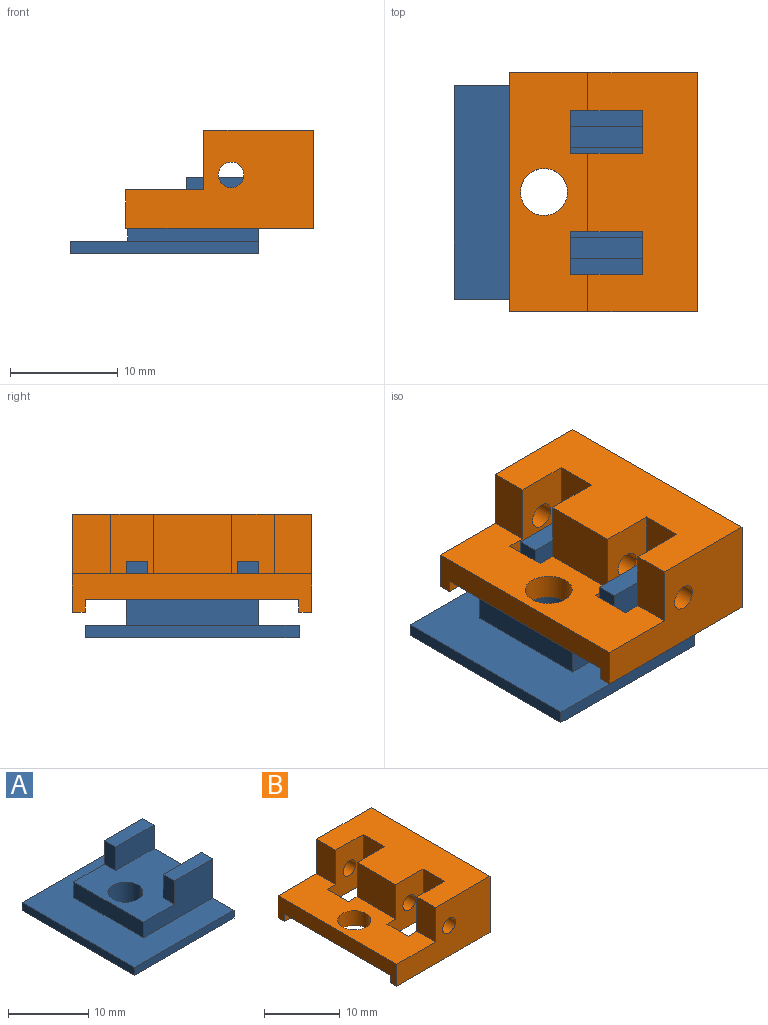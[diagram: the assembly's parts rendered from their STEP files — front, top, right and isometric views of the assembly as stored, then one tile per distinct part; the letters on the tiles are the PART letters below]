
ASSEMBLY  parts=2 mates=1
PART A: 17 faces, bbox 17.5x19.8x7.1 mm
  f0: plane 19.84x17.51mm, normal (0,0,1), area 197.6mm2, adj f1,f2,f3,f4,f7,f13,f15
  f1: plane 19.84x7.14mm, normal (1,0,0), area 67.1mm2, adj f0,f2,f4,f6,f7,f9,f10,f11
  f2: plane 17.51x1.19mm, normal (0,1,0), area 20.9mm2, adj f0,f1,f3,f6
  f3: plane 19.84x1.19mm, normal (-1,0,0), area 23.6mm2, adj f0,f2,f4,f6
  f4: plane 17.51x1.19mm, normal (0,-1,0), area 20.9mm2, adj f0,f1,f3,f6
  f5: cylinder r=2.18mm len=4.37mm, axis (0,0,-1), area 49mm2, adj f6,f16
  f6: plane 19.84x17.51mm, normal (0,0,-1), area 332.6mm2, adj f1,f2,f3,f4,f5
  f7: plane 12.18x5.95mm, normal (0,1,0), area 53.1mm2, adj f0,f1,f8,f10,f15,f16
  f8: plane 3.57x1.98mm, normal (-1,0,0), area 7.1mm2, adj f7,f9,f10,f16
  f9: plane 6.75x3.57mm, normal (0,-1,0), area 24.1mm2, adj f1,f8,f10,f16
  f10: plane 6.75x1.98mm, normal (0,0,1), area 13.4mm2, adj f1,f7,f8,f9
  f11: plane 6.75x3.57mm, normal (0,1,0), area 24.1mm2, adj f1,f12,f14,f16
  f12: plane 3.57x1.98mm, normal (-1,0,0), area 7.1mm2, adj f11,f13,f14,f16
  f13: plane 12.18x5.95mm, normal (0,-1,0), area 53.1mm2, adj f0,f1,f12,f14,f15,f16
  f14: plane 6.75x1.98mm, normal (0,0,1), area 13.4mm2, adj f1,f11,f12,f13
  f15: plane 12.3x2.38mm, normal (-1,0,0), area 29.3mm2, adj f0,f7,f13,f16
  f16: plane 12.3x12.18mm, normal (0,0,1), area 108.2mm2, adj f1,f5,f7,f8,f9,f11,f12,f13
PART B: 26 faces, bbox 17.5x22.2x9.1 mm
  f0: plane 22.23x7.25mm, normal (0,0,1), area 133.1mm2, adj f1,f2,f5,f6,f7,f8,f11,f12
  f1: plane 7.94x6.75mm, normal (0,-1,0), area 40mm2, adj f0,f3,f4,f6,f15,f16,f25
  f2: plane 7.94x6.75mm, normal (0,1,0), area 40mm2, adj f0,f3,f7,f9,f15,f16,f25
  f3: plane 19.84x17.46mm, normal (0,0,-1), area 278mm2, adj f1,f2,f4,f5,f6,f7,f8,f9
  f4: plane 7.94x3.97mm, normal (-1,0,0), area 31.5mm2, adj f1,f3,f5,f16
  f5: plane 7.94x6.75mm, normal (0,1,0), area 40mm2, adj f0,f3,f4,f6,f16,f22,f23
  f6: plane 3.97x2.38mm, normal (1,0,0), area 9.5mm2, adj f0,f1,f3,f5
  f7: plane 3.97x2.38mm, normal (1,0,0), area 9.5mm2, adj f0,f2,f3,f8
  f8: plane 7.94x6.75mm, normal (0,-1,0), area 40mm2, adj f0,f3,f7,f9,f16,f21,f24
  f9: plane 7.94x3.97mm, normal (-1,0,0), area 31.5mm2, adj f2,f3,f8,f16
  f10: plane 22.23x9.13mm, normal (1,0,0), area 179.2mm2, adj f3,f11,f13,f16,f17,f18,f19,f20
  f11: plane 17.46x9.13mm, normal (0,1,0), area 114.7mm2, adj f0,f10,f12,f16,f18,f21,f24
  f12: plane 22.23x3.57mm, normal (-1,0,0), area 55.8mm2, adj f0,f3,f11,f13,f17,f18,f19,f20
  f13: plane 17.46x9.13mm, normal (0,-1,0), area 114.7mm2, adj f0,f10,f12,f16,f20,f22,f23
  f14: cylinder r=2.18mm len=4.37mm, axis (0,0,-1), area 32.7mm2, adj f0,f3
  f15: plane 7.25x5.56mm, normal (-1,0,0), area 40.3mm2, adj f0,f1,f2,f16
  f16: plane 22.23x10.21mm, normal (0,0,1), area 186.5mm2, adj f1,f2,f4,f5,f8,f9,f10,f11
  f17: plane 17.46x1.19mm, normal (0,-1,0), area 20.8mm2, adj f3,f10,f12,f18
  f18: plane 17.46x1.19mm, normal (0,0,-1), area 20.8mm2, adj f10,f11,f12,f17
  f19: plane 17.46x1.19mm, normal (0,1,0), area 20.8mm2, adj f3,f10,f12,f20
  f20: plane 17.46x1.19mm, normal (0,0,-1), area 20.8mm2, adj f10,f12,f13,f19
  f21: plane 5.56x3.57mm, normal (-1,0,0), area 19.8mm2, adj f0,f8,f11,f16
  f22: plane 5.56x3.46mm, normal (-1,0,0), area 19.3mm2, adj f0,f5,f13,f16
  f23: cylinder r=1.19mm len=3.46mm, axis (0,1,0), area 25.9mm2, adj f5,f13
  f24: cylinder r=1.19mm len=3.57mm, axis (0,1,0), area 26.7mm2, adj f8,f11
  f25: cylinder r=1.19mm len=7.25mm, axis (0,1,0), area 54.2mm2, adj f1,f2
PLACE A t=(-3.63,-0.77,-0.47)mm fixed
PLACE B t=(-3.71,2.82,3.1)mm
MATE pin_slot B.f14 <-> A.f5  axis (0,0,-1) through (-9.27,-0.75,3.1)mm
